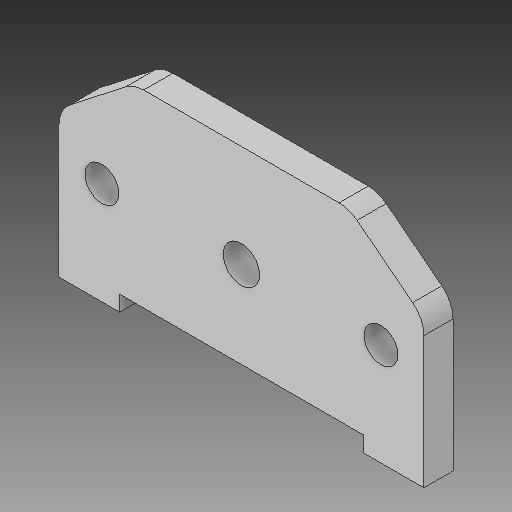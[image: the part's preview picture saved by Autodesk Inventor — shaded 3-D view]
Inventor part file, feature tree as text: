
AUTODESK INVENTOR PART (.ipt)
format: ipt  version: 2019 (Build 230136000, 136)  size: 132,608 bytes
history: native  units: mm
features: extrude x1, fillet x1, sketch x1
ambient origin geometry x8: Origin, YZ Plane, XZ Plane, XY Plane, X Axis, Y Axis, Z Axis, Center Point
bodies: Body1 (feature_tree)
feature tree (3):
  extrude  "Extrusion2"  Depth=3.2mm
  fillet  "Fillet2"  Radius=22.340214mm
  sketch  "Sketch1"  dims[d0=30.0mm d1=30.0mm d3=22.340214mm d4=75.0mm d5=7.0mm d7=7.0mm d9=28.678mm d10=28.678mm d24=7.5mm d25=6.0mm d26=0.0mm d27=6.0mm d28=50.0mm d29=12.5mm d30=3.2mm d31=37.5mm d32=22.340214mm d33=3.2mm d34=17.8mm d36=44.281401mm]
